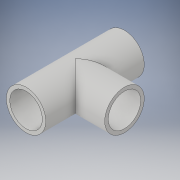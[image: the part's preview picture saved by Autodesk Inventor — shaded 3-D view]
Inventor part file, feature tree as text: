
AUTODESK INVENTOR PART (.ipt)
format: ipt  version: 2018 (Build 220112000, 112)  size: 148,992 bytes
history: native  units: in
note: dims shown in document units (in); Inventor stores cm internally (conversion verified against a paired STEP export)
features: sketch x9, extrude x8, plane x1
ambient origin geometry x8: Origin, YZ Plane, XZ Plane, XY Plane, X Axis, Y Axis, Z Axis, Center Point
bodies: Solid1 (feature_tree)
feature tree (18):
  extrude  "Extrusion1"  Depth=4.0in TaperAngle=0.0deg
  sketch  "Sketch2"  dims[d3=1.1975in d4=0.0in d5=0.8025in d6=0.0in]
  sketch  "Sketch3"  dims[d7=1.321in d8=1.0in]
  plane  "Work Plane1"
  sketch  "Sketch4"  dims[d9=1.321in d10=1.0in]
  extrude  "Extrusion2"  Depth=0.8025in TaperAngle=0.0deg
  extrude  "Extrusion3"  Depth=1.0in
  sketch  "Sketch5"  dims[d11=1.321in d12=1.248in d13=0.0in]
  sketch  "Sketch6"  dims[d14=1.248in d15=0.0in d16=1.248in d17=0.0in]
  sketch  "Sketch7"  dims[d18=4.0in d19=0.0in d20=2.0in d21=0.0in]
  sketch  "Sketch8"
  extrude  "Extrusion4"  Depth=1.0in
  extrude  "Extrusion5"  Depth=1.248in TaperAngle=0.0deg
  extrude  "Extrusion6"  Depth=1.248in TaperAngle=0.0deg
  extrude  "Extrusion7"  Depth=4.0in TaperAngle=0.0deg
  extrude  "Extrusion8"  [1 undecoded]
  sketch  "Sketch1"  dims[d0=1.605in d1=4.0in d2=0.0in]
  sketch  "Sketch9"
note: 1 required parameter value undecoded (feature->parameter linkage not recoverable at this tier; creation-order binding heuristic only, values carry confidence <= 0.55)
